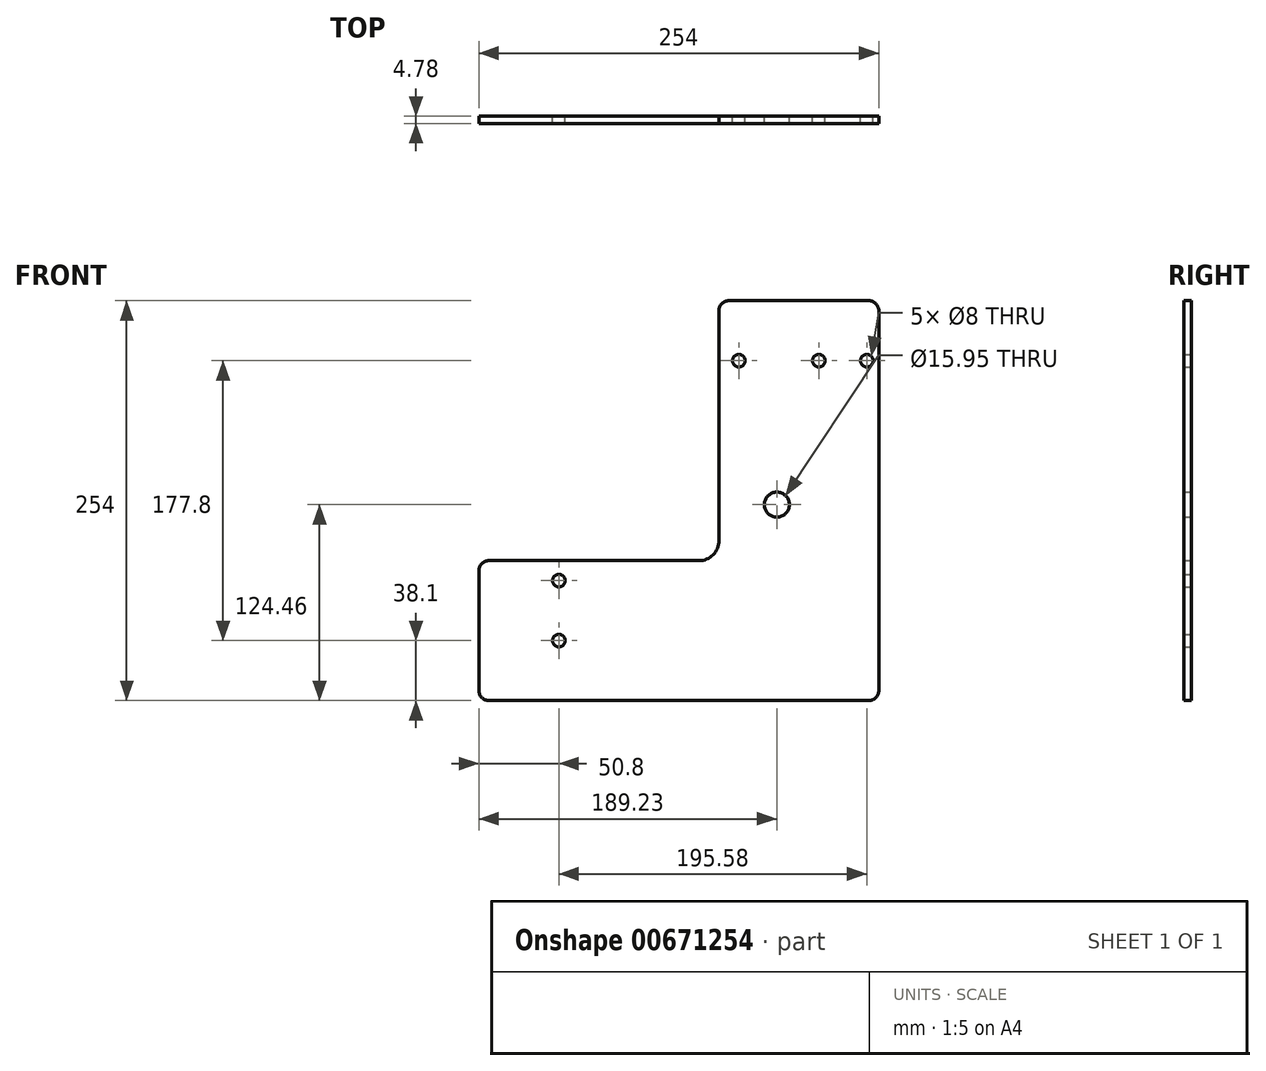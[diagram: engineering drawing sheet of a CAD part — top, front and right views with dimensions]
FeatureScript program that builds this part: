
annotation { "Feature Type Name" : "Feature", "Feature Type Description" : "" }
export const myFeature = defineFeature(function(context is Context, id is Id, definition is map)
    precondition{}
    {
        {
            var Q0;
            Q0=qCreatedBy(makeId("Front.planeOp"),FACE);
            var sketch = newSketch(context, id + "F0", { "sketchPlane" : qUnion([Q0])});
            skPoint(sketch, "E0.middle", {"position": v(0, 0) * mm});
            skLineSegment(sketch, "E1", {"start": v(0, 6.35) * mm, "end": v(0, 247.65) * mm});
            skLineSegment(sketch, "E2", {"start": v(-6.35, 254) * mm, "end": v(-95.25, 254) * mm});
            skLineSegment(sketch, "E3", {"start": v(-101.6, 247.65) * mm, "end": v(-101.6, 101.6) * mm});
            skLineSegment(sketch, "E4", {"start": v(-114.3, 88.9) * mm, "end": v(-247.65, 88.9) * mm});
            skLineSegment(sketch, "E5", {"start": v(-254, 82.55) * mm, "end": v(-254, 6.35) * mm});
            skLineSegment(sketch, "E6", {"start": v(-247.65, 0) * mm, "end": v(-6.35, 0) * mm});
            skCircle(sketch, "E7", {"center": v(-33.35, 48.26) * mm, "radius": 9.53 * mm});
            skCircle(sketch, "E8", {"center": v(-64.77, 124.46) * mm, "radius": 63.5 * mm});
            skPoint(sketch, "E9.visualSharp", {"position": v(-254, 88.9) * mm});
            skArc(sketch, "E9.filletArc", {"start": v(-247.65, 88.9) * mm, "mid": v(-252.14, 87.04) * mm, "end": v(-254, 82.55) * mm});
            skPoint(sketch, "E10.visualSharp", {"position": v(-101.6, 88.9) * mm});
            skArc(sketch, "E10.filletArc", {"start": v(-114.3, 88.9) * mm, "mid": v(-105.32, 92.62) * mm, "end": v(-101.6, 101.6) * mm});
            skPoint(sketch, "E11.visualSharp", {"position": v(-101.6, 254) * mm});
            skArc(sketch, "E11.filletArc", {"start": v(-95.25, 254) * mm, "mid": v(-99.74, 252.14) * mm, "end": v(-101.6, 247.65) * mm});
            skPoint(sketch, "E12.visualSharp", {"position": v(0, 254) * mm});
            skArc(sketch, "E12.filletArc", {"start": v(0, 247.65) * mm, "mid": v(-1.86, 252.14) * mm, "end": v(-6.35, 254) * mm});
            skPoint(sketch, "E13.visualSharp", {"position": v(-254, 0) * mm});
            skArc(sketch, "E13.filletArc", {"start": v(-254, 6.35) * mm, "mid": v(-252.14, 1.86) * mm, "end": v(-247.65, 0) * mm});
            skArc(sketch, "E14.filletArc", {"start": v(-6.35, 0) * mm, "mid": v(-1.86, 1.86) * mm, "end": v(0, 6.35) * mm});
            skCircle(sketch, "E15", {"center": v(-203.2, 76.2) * mm, "radius": 4 * mm});
            skCircle(sketch, "E16", {"center": v(-203.2, 38.1) * mm, "radius": 4 * mm});
            skCircle(sketch, "E17", {"center": v(-64.77, 124.46) * mm, "radius": 7.98 * mm});
            skCircle(sketch, "E18", {"center": v(-7.62, 215.9) * mm, "radius": 4 * mm});
            skCircle(sketch, "E19", {"center": v(-38.1, 215.9) * mm, "radius": 4 * mm});
            skCircle(sketch, "E20", {"center": v(-88.9, 215.9) * mm, "radius": 4 * mm});
            skSolve(sketch);
        }
        {
            var Q0;
            Q0=makeQuery(id+"F0.imprint","IMPRINT",FACE,{"disambiguationData":[TD([[makeQuery(id+"F0.imprint","IMPRINT",EDGE,{"derivedFrom":sQuery(id+"F0.wireOp",EDGE,"E1")}),1.0]])]});
            var Q1;
            Q1=makeQuery(id+"F0.imprint","IMPRINT",FACE,{"disambiguationData":[TD([[makeQuery(id+"F0.imprint","IMPRINT",EDGE,{"derivedFrom":sQuery(id+"F0.wireOp",EDGE,"E7")}),1.0]])]});
            var Q2;
            {var subQ0=sQuery(id+"F0.wireOp",EDGE,"E10.filletArc");Q2=makeQuery(id+"F0.imprint","IMPRINT",FACE,{"disambiguationData":[TD([[makeQuery(id+"F0.imprint","IMPRINT",EDGE,{"derivedFrom":subQ0}),-1.0]])]});}
            extrude(context, id + "F1", {"entities" : qUnion([Q0, Q1, Q2]), "depth" : 4.78 * mm, "offsetDistance" : 25.4 * mm});
        }
    });
